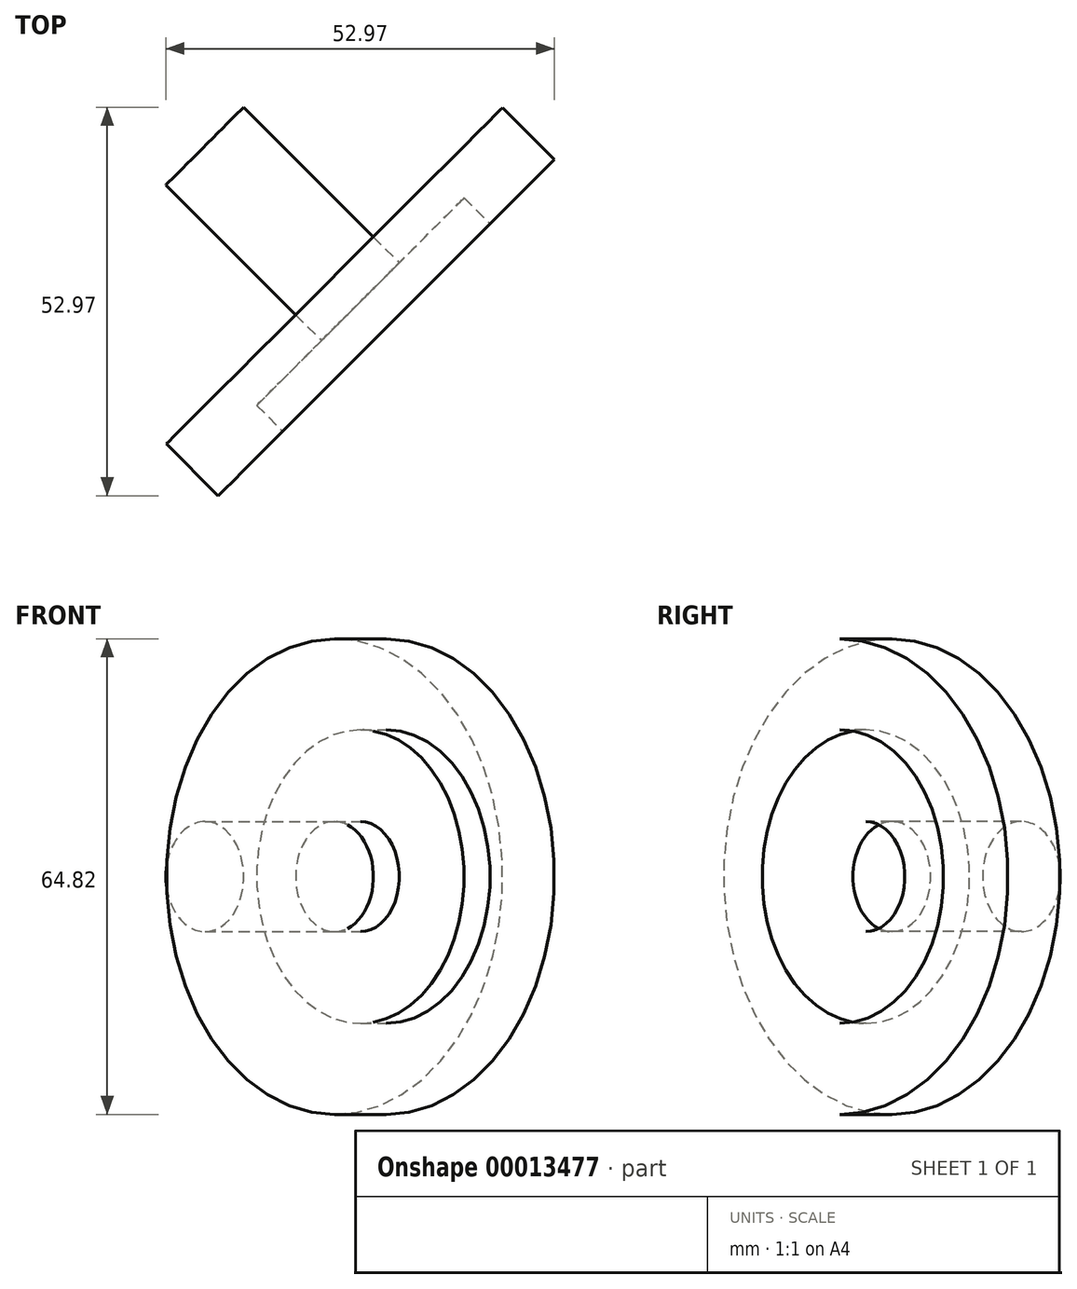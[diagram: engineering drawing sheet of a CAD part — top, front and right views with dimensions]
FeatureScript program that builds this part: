
annotation { "Feature Type Name" : "Feature", "Feature Type Description" : "" }
export const myFeature = defineFeature(function(context is Context, id is Id, definition is map)
    precondition{}
    {
        {
            var Q0;
            Q0=qCreatedBy(makeId("Front.planeOp"),FACE);
            var sketch = newSketch(context, id + "F0", { "sketchPlane" : qUnion([Q0])});
            skLineSegment(sketch, "E0", {"start": v(0, 0) * mm, "end": v(40.52, 0) * mm, "construction": true});
            skPoint(sketch, "E1.orphan", {"position": v(35.4, 4) * mm});
            skCircle(sketch, "E2.converted", {"center": v(0, 0) * mm, "radius": 32.4 * mm});
            skSolve(sketch);
        }
        {
            var Q0;
            Q0=makeQuery(id+"F0.imprint","IMPRINT",FACE,{"disambiguationData":[TD([[makeQuery(id+"F0.imprint","IMPRINT",EDGE,{"derivedFrom":sQuery(id+"F0.wireOp",EDGE,"E2.converted")}),1.0]])]});
            extrude(context, id + "F1", {"entities" : qUnion([Q0]), "oppositeDirection" : true, "depth" : 10 * mm});
        }
        {
            var Q0;
            Q0=makeQuery(id+"F1.opExtrude","CAP_FACE",FACE,{"disambiguationData":[OSD([sQuery(id+"F0.wireOp",EDGE,"E2.converted")])],"isStart":true});
            var sketch = newSketch(context, id + "F2", { "sketchPlane" : qUnion([Q0])});
            skCircle(sketch, "E3", {"center": v(0, 0) * mm, "radius": 20 * mm});
            skCircle(sketch, "E4", {"center": v(0, 0) * mm, "radius": 7.5 * mm});
            skSolve(sketch);
        }
        {
            var Q0;
            Q0=makeQuery(id+"F2.imprint","IMPRINT",FACE,{"disambiguationData":[TD([[makeQuery(id+"F2.imprint","IMPRINT",EDGE,{"derivedFrom":sQuery(id+"F2.wireOp",EDGE,"E3")}),1.0]])]});
            var Q1;
            Q1=makeQuery(id+"F1.opExtrude","CAP_FACE",FACE,{"disambiguationData":[OSD([sQuery(id+"F0.wireOp",EDGE,"E2.converted")])],"isStart":false});
            extrude(context, id + "F3", {"entities" : qUnion([Q0]), "operationType" : NewBodyOperationType.REMOVE, "oppositeDirection" : true, "endBoundEntity" : qUnion([Q1]), "depth" : 5 * mm});
        }
        {
            var Q0;
            Q0=makeQuery(id+"F3.boolean.opBoolean","SPLIT",FACE,{"disambiguationData":[TD([makeQuery(id+"F3.opExtrude","SWEPT_FACE",FACE,{"disambiguationData":[OSD([sQuery(id+"F2.wireOp",EDGE,"E4")])]})])],"derivedFrom":makeQuery(id+"F1.opExtrude","CAP_FACE",FACE,{"disambiguationData":[OSD([sQuery(id+"F0.wireOp",EDGE,"E2.converted")])],"isStart":true})});
            var Q1;
            Q1=makeQuery(id+"F3.boolean.opBoolean","SPLIT",FACE,{"disambiguationData":[TD([makeQuery(id+"F3.opExtrude","SWEPT_FACE",FACE,{"disambiguationData":[OSD([sQuery(id+"F2.wireOp",EDGE,"E4")])]})])],"derivedFrom":makeQuery(id+"F1.opExtrude","CAP_FACE",FACE,{"disambiguationData":[OSD([sQuery(id+"F0.wireOp",EDGE,"E2.converted")])],"isStart":true})});
            extrude(context, id + "F4", {"entities" : qUnion([Q0]), "oppositeDirection" : true, "endBoundEntity" : qUnion([Q1]), "depth" : 35 * mm});
        }
        {
            var Q0;
            Q0=makeQuery(id+"F3.boolean.opBoolean","SPLIT",FACE,{"disambiguationData":[TD([makeQuery(id+"F3.opExtrude","SWEPT_FACE",FACE,{"disambiguationData":[OSD([sQuery(id+"F2.wireOp",EDGE,"E4")])]})])],"derivedFrom":makeQuery(id+"F1.opExtrude","CAP_FACE",FACE,{"disambiguationData":[OSD([sQuery(id+"F0.wireOp",EDGE,"E2.converted")])],"isStart":true})});
            var Q1;
            Q1=makeQuery(id+"F3.boolean.opBoolean","COPY",FACE,{"derivedFrom":makeQuery(id+"F3.opExtrude","CAP_FACE",FACE,{"disambiguationData":[OSD([sQuery(id+"F2.wireOp",EDGE,"E3"),sQuery(id+"F2.wireOp",EDGE,"E4")])],"isStart":false})});
            extrude(context, id + "F5", {"entities" : qUnion([Q0]), "operationType" : NewBodyOperationType.REMOVE, "endBound" : BoundingType.UP_TO_NEXT, "oppositeDirection" : true, "endBoundEntity" : qUnion([Q1]), "depth" : 25 * mm});
        }
        {
            var Q0;
            Q0=qCreatedBy(makeId("Front.planeOp"),FACE);
            var sketch = newSketch(context, id + "F6", { "sketchPlane" : qUnion([Q0])});
            skLineSegment(sketch, "E5", {"start": v(0, -2.25) * mm, "end": v(0, 63.06) * mm, "construction": true});
            skSolve(sketch);
        }
        {
            var Q0;
            Q0=makeQuery(id+"F1.opExtrude","SWEPT_BODY",BODY,{"disambiguationData":[OSD([sQuery(id+"F0.wireOp",EDGE,"E2.converted")])]});
            var Q1;
            Q1=makeQuery(id+"F4.opExtrude","SWEPT_BODY",BODY,{"disambiguationData":[OSD([sQuery(id+"F0.wireOp",EDGE,"E2.converted")])]});
            var Q2;
            Q2=sQuery(id+"F6.wireOp",EDGE,"E5");
            var Q3;
            Q3=sQuery(id+"F6.wireOp",EDGE,"E5");
            transform(context, id + "F7", {"entities" : qUnion([Q0, Q1]), "transformType" : TransformType.ROTATION, "transformAxis" : qUnion([Q3]), "angle" : 45 * degree, "makeCopy" : false});
        }
    });
